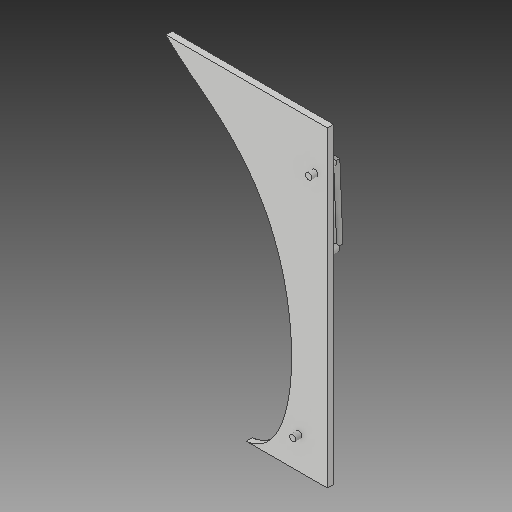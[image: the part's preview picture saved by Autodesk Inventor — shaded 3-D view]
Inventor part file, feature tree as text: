
AUTODESK INVENTOR PART (.ipt)
format: ipt  version: 2018 (Build 220112000, 112)  size: 150,528 bytes
history: native  units: in
note: dims shown in document units (in); Inventor stores cm internally (conversion verified against a paired STEP export)
features: sketch x6, other x3
ambient origin geometry x8: Origin, YZ Plane, XZ Plane, XY Plane, X Axis, Y Axis, Z Axis, Center Point
bodies: Solid1 (feature_tree)
feature tree (9):
  other  "side frame"
  other  "Solid1::side frame"
  other  "TaggingFeature1"
  sketch  "Sketch1"  dims[d0=0.3937in]
  sketch  "Sketch2"
  sketch  "Sketch3"
  sketch  "Sketch4"
  sketch  "Sketch6"
  sketch  "Sketch8"
